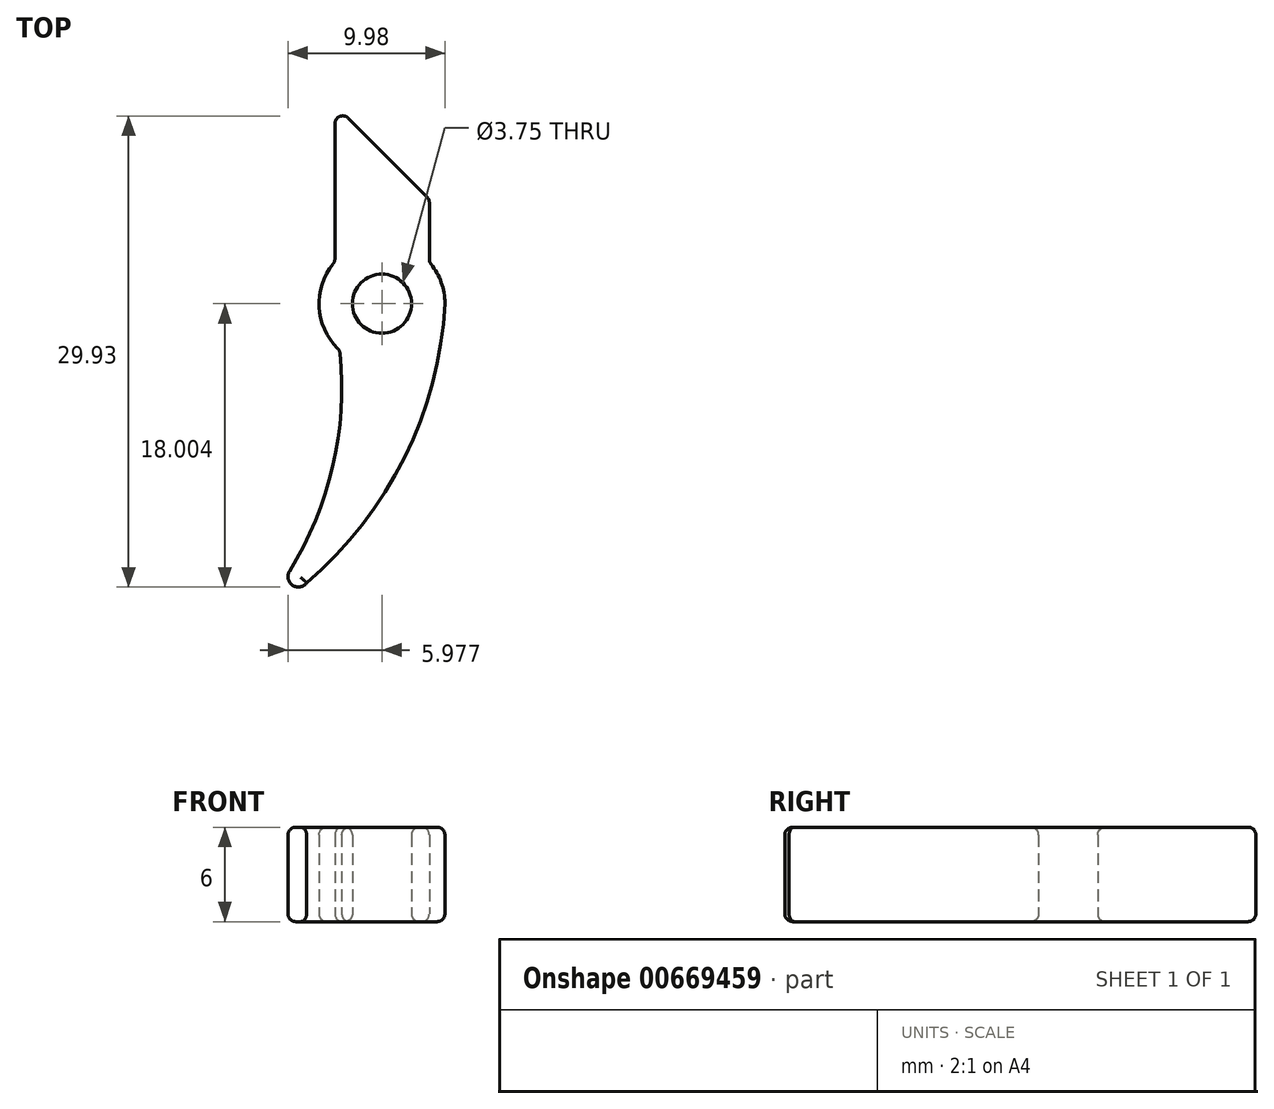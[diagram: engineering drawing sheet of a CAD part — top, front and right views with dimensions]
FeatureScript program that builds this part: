
annotation { "Feature Type Name" : "Feature", "Feature Type Description" : "" }
export const myFeature = defineFeature(function(context is Context, id is Id, definition is map)
    precondition{}
    {
        {
            var Q0;
            Q0=qCreatedBy(makeId("Top.planeOp"),FACE);
            var sketch = newSketch(context, id + "F0", { "sketchPlane" : qUnion([Q0])});
            skCircle(sketch, "E0", {"center": v(0.69, 0.08) * mm, "radius": 4 * mm});
            skCircle(sketch, "E1", {"center": v(0.69, 0.08) * mm, "radius": 1.88 * mm});
            skArc(sketch, "E2", {"start": v(-5.2, -16.93) * mm, "mid": v(-2.42, -10.17) * mm, "end": v(-2, -2.88) * mm});
            skArc(sketch, "E3", {"start": v(-4.1, -17.64) * mm, "mid": v(2.13, -9.68) * mm, "end": v(4.69, 0.1) * mm});
            skLineSegment(sketch, "E4.bottom", {"start": v(-2.3, 6.72) * mm, "end": v(3.7, 6.72) * mm});
            skLineSegment(sketch, "E4.left", {"start": v(-2.3, 6.72) * mm, "end": v(-2.3, 2.74) * mm});
            skLineSegment(sketch, "E4.right", {"start": v(3.7, 6.72) * mm, "end": v(3.7, 2.72) * mm});
            skPoint(sketch, "E4.middle", {"position": v(0.69, 3.08) * mm});
            skLineSegment(sketch, "E5", {"start": v(-2.3, 6.72) * mm, "end": v(-2.3, 12.72) * mm});
            skLineSegment(sketch, "E6", {"start": v(-2.3, 12.72) * mm, "end": v(3.7, 6.72) * mm});
            skArc(sketch, "E7", {"start": v(-5.2, -16.93) * mm, "mid": v(-4.99, -17.81) * mm, "end": v(-4.1, -17.64) * mm});
            skSolve(sketch);
        }
        {
            var Q0;
            Q0=makeQuery(id+"F0.imprint","IMPRINT",FACE,{"disambiguationData":[TD([[makeQuery(id+"F0.imprint","IMPRINT",EDGE,{"derivedFrom":sQuery(id+"F0.wireOp",EDGE,"E4.bottom")}),1.0]])]});
            var Q1;
            Q1=makeQuery(id+"F0.imprint","IMPRINT",FACE,{"disambiguationData":[TD([[makeQuery(id+"F0.imprint","IMPRINT",EDGE,{"derivedFrom":sQuery(id+"F0.wireOp",EDGE,"E4.bottom")}),-1.0]])]});
            var Q2;
            Q2=makeQuery(id+"F0.imprint","IMPRINT",FACE,{"disambiguationData":[TD([[makeQuery(id+"F0.imprint","IMPRINT",EDGE,{"derivedFrom":sQuery(id+"F0.wireOp",EDGE,"E1")}),-1.0]])]});
            var Q3;
            {var subQ0=sQuery(id+"F0.wireOp",EDGE,"E2");Q3=makeQuery(id+"F0.imprint","IMPRINT",FACE,{"disambiguationData":[TD([[makeQuery(id+"F0.imprint","IMPRINT",EDGE,{"derivedFrom":subQ0}),-1.0]])]});}
            extrude(context, id + "F1", {"entities" : qUnion([Q0, Q1, Q2, Q3]), "depth" : 6 * mm, "offsetDistance" : 25 * mm});
        }
        {
            var Q0;
            Q0=makeQuery(id+"F1.opExtrude","CAP_FACE",FACE,{"disambiguationData":[OSD([sQuery(id+"F0.wireOp",EDGE,"E0"),sQuery(id+"F0.wireOp",EDGE,"E1"),sQuery(id+"F0.wireOp",EDGE,"E2"),sQuery(id+"F0.wireOp",EDGE,"E3"),sQuery(id+"F0.wireOp",EDGE,"E4.left"),sQuery(id+"F0.wireOp",EDGE,"E4.right"),sQuery(id+"F0.wireOp",EDGE,"E5"),sQuery(id+"F0.wireOp",EDGE,"E6"),sQuery(id+"F0.wireOp",EDGE,"E7")])],"isStart":false});
            var Q1;
            Q1=makeQuery(id+"F1.opExtrude","CAP_FACE",FACE,{"disambiguationData":[OSD([sQuery(id+"F0.wireOp",EDGE,"E0"),sQuery(id+"F0.wireOp",EDGE,"E1"),sQuery(id+"F0.wireOp",EDGE,"E2"),sQuery(id+"F0.wireOp",EDGE,"E3"),sQuery(id+"F0.wireOp",EDGE,"E4.left"),sQuery(id+"F0.wireOp",EDGE,"E4.right"),sQuery(id+"F0.wireOp",EDGE,"E5"),sQuery(id+"F0.wireOp",EDGE,"E6"),sQuery(id+"F0.wireOp",EDGE,"E7")])],"isStart":true});
            var Q2;
            Q2=makeQuery(id+"F1.opExtrude","SWEPT_FACE",FACE,{"disambiguationData":[OSD([sQuery(id+"F0.wireOp",EDGE,"E2")])]});
            var Q3;
            {var subQ0=sQuery(id+"F0.wireOp",EDGE,"E0");Q3=makeQuery(id+"F1.opExtrude","SWEPT_FACE",FACE,{"disambiguationData":[OSD([subQ0]),TDD([makeQuery(id+"F0.imprint","IMPRINT",EDGE,{"disambiguationData":[TD([[makeQuery(id+"F0.imprint","INTERSECT",VERTEX,{"derivedFrom":[subQ0,sQuery(id+"F0.wireOp",EDGE,"E2")]}),1.0]])],"derivedFrom":subQ0})])]});}
            var Q4;
            Q4=makeQuery(id+"F1.opExtrude","SWEPT_FACE",FACE,{"disambiguationData":[OSD([sQuery(id+"F0.wireOp",EDGE,"E4.left"),sQuery(id+"F0.wireOp",EDGE,"E5")])]});
            var Q5;
            Q5=makeQuery(id+"F1.opExtrude","SWEPT_FACE",FACE,{"disambiguationData":[OSD([sQuery(id+"F0.wireOp",EDGE,"E6")])]});
            var Q6;
            Q6=makeQuery(id+"F1.opExtrude","SWEPT_EDGE",EDGE,{"disambiguationData":[OSD([sQuery(id+"F0.wireOp",EDGE,"E0"),sQuery(id+"F0.wireOp",EDGE,"E4.right")])]});
            var Q7;
            Q7=makeQuery(id+"F1.opExtrude","SWEPT_EDGE",EDGE,{"disambiguationData":[OSD([sQuery(id+"F0.wireOp",EDGE,"E0"),sQuery(id+"F0.wireOp",EDGE,"E3")])]});
            fillet(context, id + "F2", {"entities" : qUnion([Q0, Q1, Q2, Q3, Q4, Q5, Q6, Q7]), "radius" : .5 * mm, "tangentPropagation" : true, "allowEdgeOverflow" : false});
        }
    });
